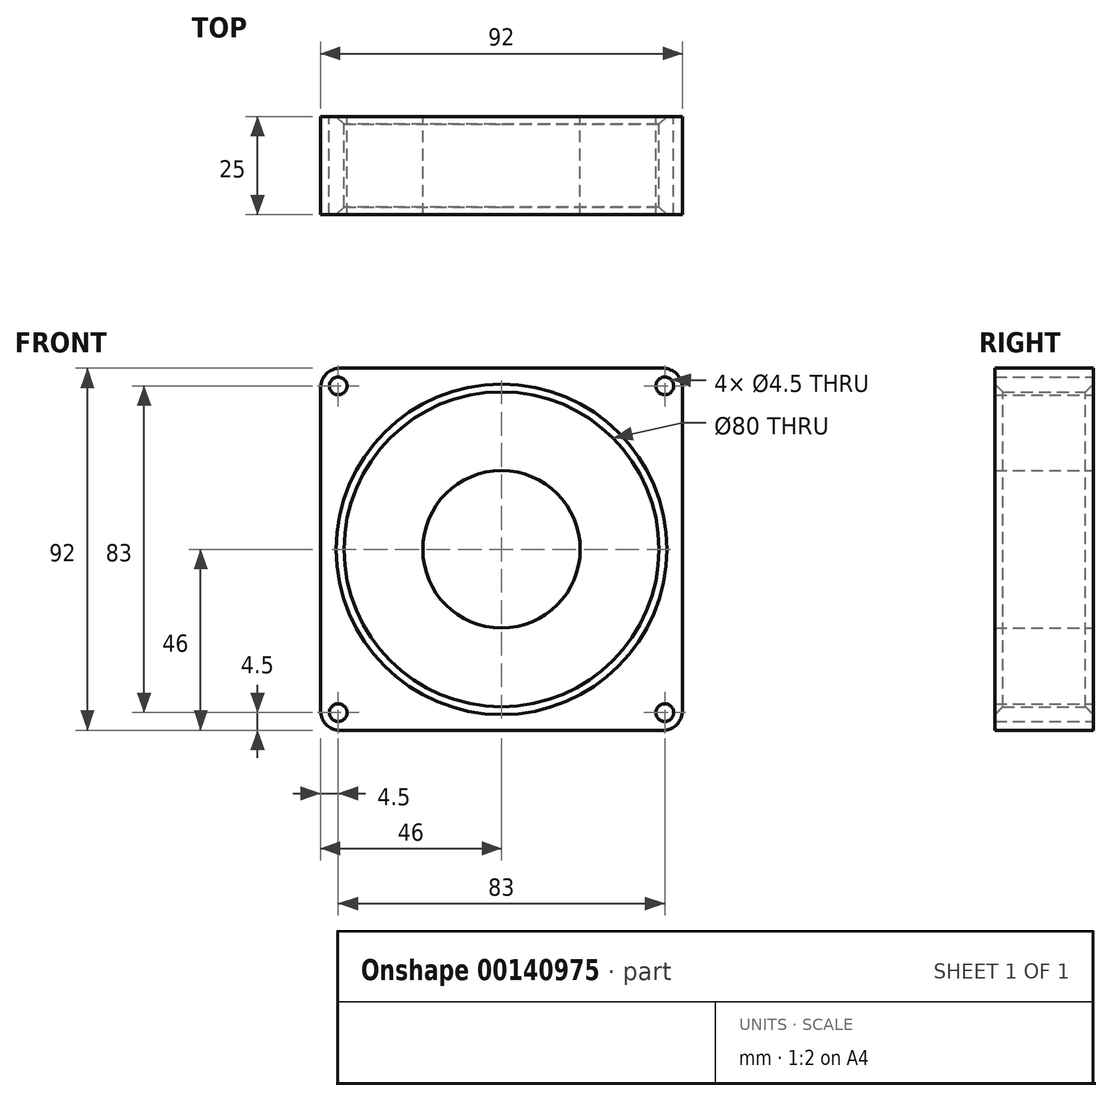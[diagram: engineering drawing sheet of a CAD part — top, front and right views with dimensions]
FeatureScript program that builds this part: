
annotation { "Feature Type Name" : "Feature", "Feature Type Description" : "" }
export const myFeature = defineFeature(function(context is Context, id is Id, definition is map)
    precondition{}
    {
        {
            var Q0;
            Q0=qCreatedBy(makeId("Front.planeOp"),FACE);
            var sketch = newSketch(context, id + "F0", { "sketchPlane" : qUnion([Q0])});
            skLineSegment(sketch, "E0.bottom", {"start": v(-46, 46) * mm, "end": v(46, 46) * mm});
            skLineSegment(sketch, "E0.top", {"start": v(-46, -46) * mm, "end": v(46, -46) * mm});
            skLineSegment(sketch, "E0.left", {"start": v(-46, 46) * mm, "end": v(-46, -46) * mm});
            skLineSegment(sketch, "E0.right", {"start": v(46, 46) * mm, "end": v(46, -46) * mm});
            skPoint(sketch, "E1", {"position": v(0, 46) * mm});
            skPoint(sketch, "E2", {"position": v(-46, 0) * mm});
            skCircle(sketch, "E3", {"center": v(-41.5, 41.5) * mm, "radius": 2.25 * mm});
            skCircle(sketch, "E4", {"center": v(0, 0) * mm, "radius": 40 * mm});
            skCircle(sketch, "E5", {"center": v(0, 0) * mm, "radius": 20 * mm});
            skCircle(sketch, "E6.MirrorC", {"center": v(41.5, 41.5) * mm, "radius": 2.25 * mm});
            skCircle(sketch, "E7.MirrorC", {"center": v(-41.5, -41.5) * mm, "radius": 2.25 * mm});
            skCircle(sketch, "E8.MirrorC", {"center": v(41.5, -41.5) * mm, "radius": 2.25 * mm});
            skSolve(sketch);
        }
        {
            var Q0;
            Q0 = qSketchRegion(id + "F0", true);
            var Q1;
            Q1=makeQuery(id+"F0.imprint","IMPRINT",FACE,{"disambiguationData":[TD([[makeQuery(id+"F0.imprint","IMPRINT",EDGE,{"derivedFrom":sQuery(id+"F0.wireOp",EDGE,"E5")}),1.0]])]});
            extrude(context, id + "F1", {"entities" : qUnion([Q0, Q1]), "depth" : 25 * mm});
        }
        {
            var Q0;
            Q0=makeQuery(id+"F1.opExtrude","SWEPT_EDGE",EDGE,{"disambiguationData":[OSD([sQuery(id+"F0.wireOp",EDGE,"E0.bottom"),sQuery(id+"F0.wireOp",EDGE,"E0.right")])]});
            var Q1;
            Q1=makeQuery(id+"F1.opExtrude","SWEPT_EDGE",EDGE,{"disambiguationData":[OSD([sQuery(id+"F0.wireOp",EDGE,"E0.bottom"),sQuery(id+"F0.wireOp",EDGE,"E0.left")])]});
            var Q2;
            Q2=makeQuery(id+"F1.opExtrude","SWEPT_EDGE",EDGE,{"disambiguationData":[OSD([sQuery(id+"F0.wireOp",EDGE,"E0.top"),sQuery(id+"F0.wireOp",EDGE,"E0.right")])]});
            var Q3;
            Q3=makeQuery(id+"F1.opExtrude","SWEPT_EDGE",EDGE,{"disambiguationData":[OSD([sQuery(id+"F0.wireOp",EDGE,"E0.top"),sQuery(id+"F0.wireOp",EDGE,"E0.left")])]});
            fillet(context, id + "F2", {"entities" : qUnion([Q0, Q1, Q2, Q3]), "radius" : 5 * mm, "tangentPropagation" : true, "allowEdgeOverflow" : false});
        }
        {
            var Q0;
            Q0=makeQuery(id+"F1.opExtrude","CAP_EDGE",EDGE,{"disambiguationData":[OSD([sQuery(id+"F0.wireOp",EDGE,"E4")])],"isStart":false});
            var Q1;
            Q1=makeQuery(id+"F1.opExtrude","CAP_EDGE",EDGE,{"disambiguationData":[OSD([sQuery(id+"F0.wireOp",EDGE,"E4")])],"isStart":true});
            chamfer(context, id + "F3", {"entities" : qUnion([Q0, Q1]), "width" : 2 * mm, "tangentPropagation" : true});
        }
    });
